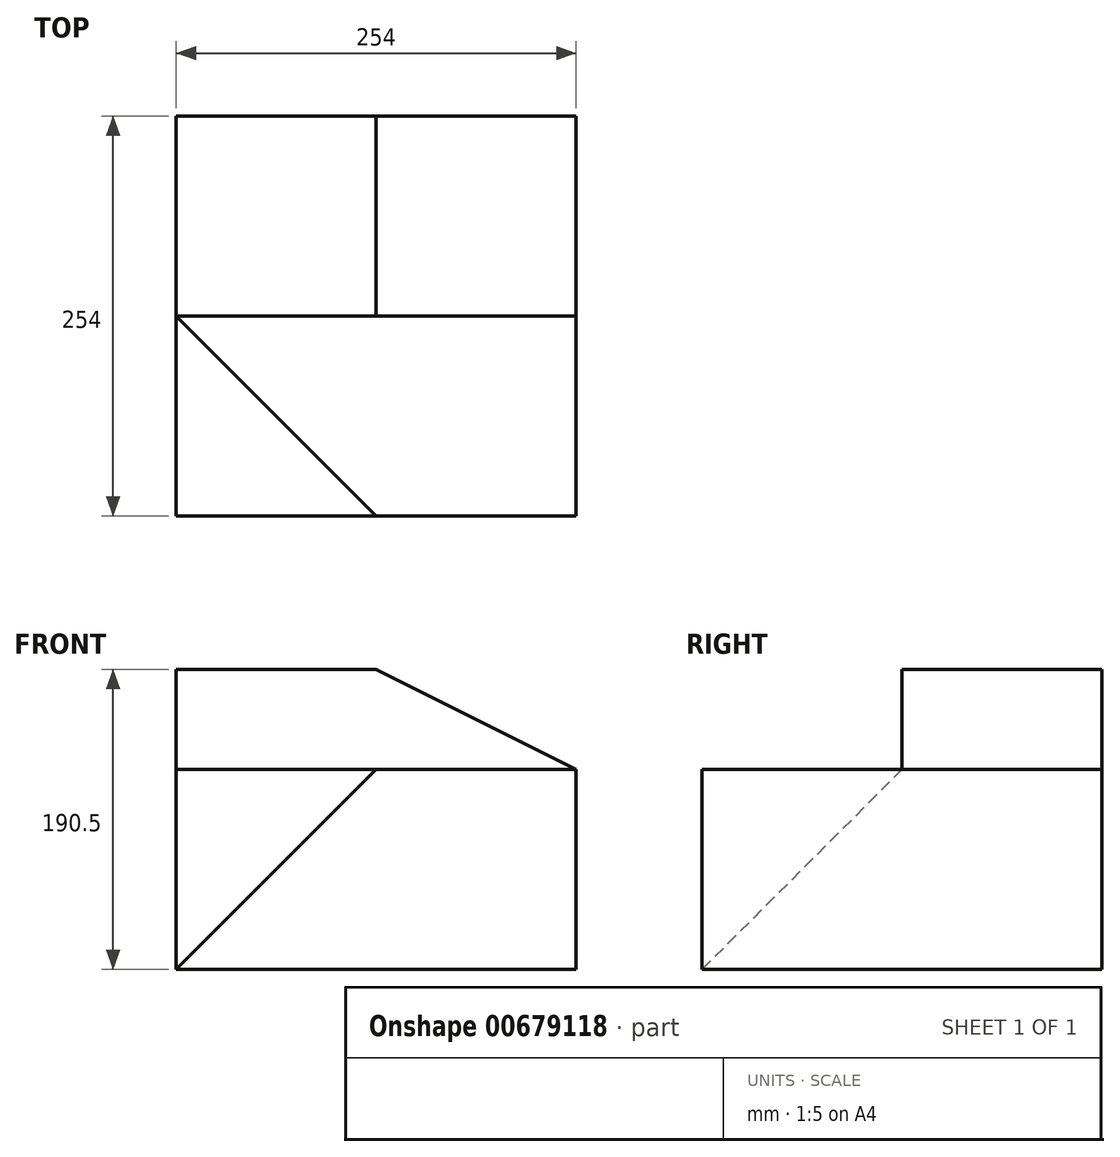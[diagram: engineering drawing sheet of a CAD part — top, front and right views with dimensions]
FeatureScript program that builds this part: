
annotation { "Feature Type Name" : "Feature", "Feature Type Description" : "" }
export const myFeature = defineFeature(function(context is Context, id is Id, definition is map)
    precondition{}
    {
        {
            var Q0;
            Q0=qCreatedBy(makeId("Front.planeOp"),FACE);
            var sketch = newSketch(context, id + "F0", { "sketchPlane" : qUnion([Q0])});
            skLineSegment(sketch, "E0", {"start": v(0, 0) * mm, "end": v(0, 190.5) * mm});
            skLineSegment(sketch, "E1", {"start": v(0, 190.5) * mm, "end": v(127, 190.5) * mm});
            skLineSegment(sketch, "E2", {"start": v(127, 190.5) * mm, "end": v(254, 127) * mm});
            skLineSegment(sketch, "E3", {"start": v(254, 127) * mm, "end": v(254, 0) * mm});
            skLineSegment(sketch, "E4", {"start": v(254, 0) * mm, "end": v(0, 0) * mm});
            skLineSegment(sketch, "E5", {"start": v(254, 127) * mm, "end": v(0, 127) * mm});
            skSolve(sketch);
        }
        {
            var Q0;
            Q0=qCreatedBy(makeId("Right.planeOp"),FACE);
            var sketch = newSketch(context, id + "F1", { "sketchPlane" : qUnion([Q0])});
            skLineSegment(sketch, "E6", {"start": v(0, 127) * mm, "end": v(-254, 127) * mm});
            skLineSegment(sketch, "E7", {"start": v(-254, 127) * mm, "end": v(-254, 0) * mm});
            skLineSegment(sketch, "E8", {"start": v(-254, 0) * mm, "end": v(0, 0) * mm});
            skLineSegment(sketch, "E9", {"start": v(0, 0) * mm, "end": v(0, 127) * mm});
            skLineSegment(sketch, "E10", {"start": v(0, 190.5) * mm, "end": v(-127, 190.5) * mm});
            skLineSegment(sketch, "E11", {"start": v(-127, 190.5) * mm, "end": v(-127, 127) * mm});
            skLineSegment(sketch, "E12", {"start": v(-127, 127) * mm, "end": v(-254, 0) * mm});
            skSolve(sketch);
        }
        {
            var Q0;
            Q0=qCreatedBy(makeId("Top.planeOp"),FACE);
            var sketch = newSketch(context, id + "F2", { "sketchPlane" : qUnion([Q0])});
            skLineSegment(sketch, "E13", {"start": v(0, 0) * mm, "end": v(127, 0) * mm});
            skLineSegment(sketch, "E14", {"start": v(127, 0) * mm, "end": v(254, 0) * mm});
            skLineSegment(sketch, "E15", {"start": v(254, 0) * mm, "end": v(254, -127) * mm});
            skLineSegment(sketch, "E16", {"start": v(254, -127) * mm, "end": v(254, -254) * mm});
            skLineSegment(sketch, "E17", {"start": v(254, -254) * mm, "end": v(0, -254) * mm});
            skLineSegment(sketch, "E18", {"start": v(0, -254) * mm, "end": v(0, -127) * mm});
            skLineSegment(sketch, "E19", {"start": v(0, -127) * mm, "end": v(0, 0) * mm});
            skLineSegment(sketch, "E20", {"start": v(0, -127) * mm, "end": v(127, -254) * mm});
            skLineSegment(sketch, "E21", {"start": v(127, -254) * mm, "end": v(0, -127) * mm});
            skLineSegment(sketch, "E22", {"start": v(254, -127) * mm, "end": v(0, -127) * mm});
            skLineSegment(sketch, "E23", {"start": v(127, 0) * mm, "end": v(127, -127) * mm});
            skSolve(sketch);
        }
        {
            var Q0;
            {var subQ0=sQuery(id+"F0.wireOp",EDGE,"E1");Q0=makeQuery(id+"F0.imprint","IMPRINT",FACE,{"disambiguationData":[TD([[makeQuery(id+"F0.imprint","IMPRINT",EDGE,{"derivedFrom":subQ0}),-1.0]])]});}
            extrude(context, id + "F3", {"entities" : qUnion([Q0]), "depth" : 127 * mm, "offsetDistance" : 25.4 * mm});
        }
        {
            var Q0;
            {var subQ1=sQuery(id+"F2.wireOp",EDGE,"E16");Q0=makeQuery(id+"F2.imprint","IMPRINT",FACE,{"disambiguationData":[TD([[makeQuery(id+"F2.imprint","IMPRINT",EDGE,{"derivedFrom":subQ1}),-1.0]])]});}
            var Q1;
            Q1=makeQuery(id+"F2.imprint","IMPRINT",FACE,{"disambiguationData":[TD([[makeQuery(id+"F2.imprint","IMPRINT",EDGE,{"derivedFrom":sQuery(id+"F2.wireOp",EDGE,"E14")}),-1.0]])]});
            var Q2;
            Q2=makeQuery(id+"F2.imprint","IMPRINT",FACE,{"disambiguationData":[TD([[makeQuery(id+"F2.imprint","IMPRINT",EDGE,{"derivedFrom":sQuery(id+"F2.wireOp",EDGE,"E13")}),-1.0]])]});
            var Q3;
            {var subQ0=sQuery(id+"F2.wireOp",EDGE,"E18");Q3=makeQuery(id+"F2.imprint","IMPRINT",FACE,{"disambiguationData":[TD([[makeQuery(id+"F2.imprint","IMPRINT",EDGE,{"derivedFrom":subQ0}),-1.0]])]});}
            extrude(context, id + "F4", {"entities" : qUnion([Q0, Q1, Q2, Q3]), "operationType" : NewBodyOperationType.ADD, "depth" : 127 * mm, "offsetDistance" : 25.4 * mm});
        }
        {
            var Q0;
            Q0=makeQuery(id+"F4.opExtrude","CAP_EDGE",EDGE,{"disambiguationData":[OSD([sQuery(id+"F2.wireOp",EDGE,"E17")])],"isStart":false});
            cPoint(context, id + "F5", {"entities" : qUnion([Q0]), "parameter" : 0.5});
        }
        {
            var Q0;
            Q0=sQuery(id+"F1.wireOp",VERTEX,"E12.start");
            var Q1;
            Q1 = qCreatedBy(id + "F5" ,VERTEX);
            var Q2;
            Q2=sQuery(id+"F1.wireOp",VERTEX,"E8.start");
            cPlane(context, id + "F6", {"entities" : qUnion([Q0, Q1, Q2]), "cplaneType" : CPlaneType.THREE_POINT, "offset" : 25.4 * mm, "width" : 152.4 * mm, "height" : 152.4 * mm});
        }
        {
            var Q0;
            Q0=qCreatedBy(id+"F6.planeOp",FACE);
            var sketch = newSketch(context, id + "F7", { "sketchPlane" : qUnion([Q0])});
            skLineSegment(sketch, "E24", {"start": v(103.7, -179.6) * mm, "end": v(103.7, 0) * mm});
            skLineSegment(sketch, "E25", {"start": v(103.7, 0) * mm, "end": v(259.24, -89.8) * mm});
            skLineSegment(sketch, "E26", {"start": v(259.24, -89.8) * mm, "end": v(103.7, -179.6) * mm});
            skSolve(sketch);
        }
        {
            var Q0;
            Q0=makeQuery(id+"F7.imprint","IMPRINT",FACE,{"disambiguationData":[TD([[makeQuery(id+"F7.imprint","IMPRINT",EDGE,{"derivedFrom":sQuery(id+"F7.wireOp",EDGE,"E24")}),-1.0]])]});
            extrude(context, id + "F8", {"entities" : qUnion([Q0]), "operationType" : NewBodyOperationType.REMOVE, "depth" : 1092.2 * mm, "offsetDistance" : 25.4 * mm});
        }
    });
